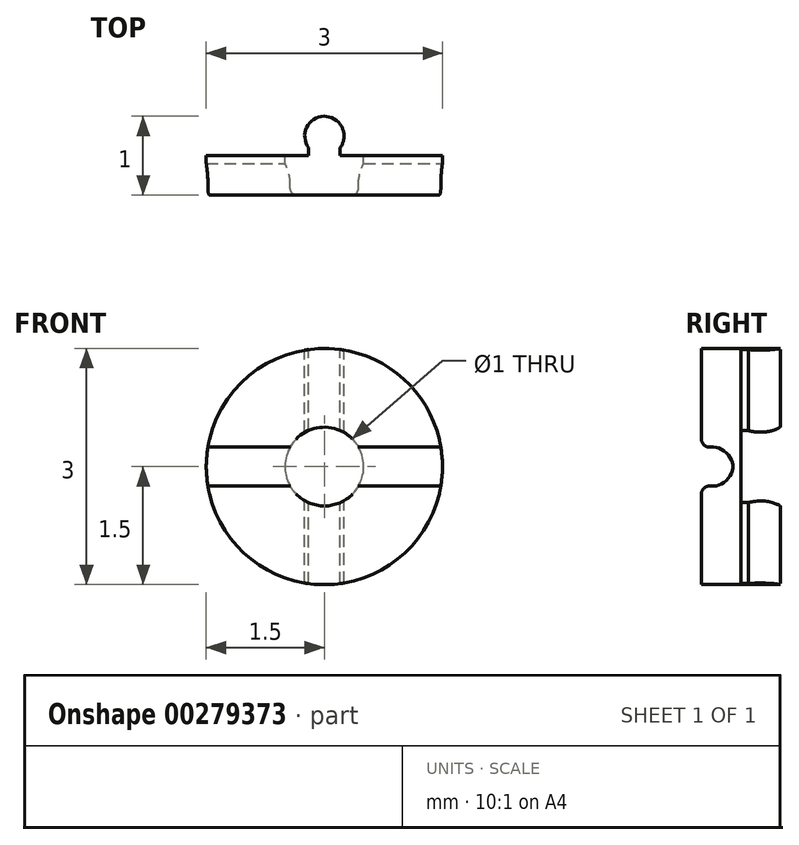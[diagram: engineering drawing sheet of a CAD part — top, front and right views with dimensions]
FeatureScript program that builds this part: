
annotation { "Feature Type Name" : "Feature", "Feature Type Description" : "" }
export const myFeature = defineFeature(function(context is Context, id is Id, definition is map)
    precondition{}
    {
        {
            var Q0;
            Q0=qCreatedBy(makeId("Front.planeOp"),FACE);
            var sketch = newSketch(context, id + "F0", { "sketchPlane" : qUnion([Q0])});
            skCircle(sketch, "E0", {"center": v(0, 0) * mm, "radius": 1.5 * mm});
            skSolve(sketch);
        }
        {
            var Q0;
            Q0 = qSketchRegion(id + "F0", true);
            extrude(context, id + "F1", {"entities" : qUnion([Q0]), "depth" : 1 * mm});
        }
        {
            var Q0;
            Q0=qCreatedBy(makeId("Top.planeOp"),FACE);
            var sketch = newSketch(context, id + "F2", { "sketchPlane" : qUnion([Q0])});
            skArc(sketch, "E1", {"start": v(0.2, -0.4) * mm, "mid": v(0, 0) * mm, "end": v(-0.2, -0.4) * mm});
            skLineSegment(sketch, "E2", {"start": v(0.2, -0.4) * mm, "end": v(1.99, -0.4) * mm});
            skLineSegment(sketch, "E3", {"start": v(1.99, -0.4) * mm, "end": v(1.99, 1) * mm});
            skLineSegment(sketch, "E4", {"start": v(1.99, 1) * mm, "end": v(-1.99, 0.99) * mm});
            skLineSegment(sketch, "E5", {"start": v(-1.99, 0.99) * mm, "end": v(-1.99, -0.4) * mm});
            skLineSegment(sketch, "E6", {"start": v(-1.99, -0.4) * mm, "end": v(-0.2, -0.4) * mm});
            skSolve(sketch);
        }
        {
            var Q0;
            Q0 = qSketchRegion(id + "F2", true);
            extrude(context, id + "F3", {"entities" : qUnion([Q0]), "operationType" : NewBodyOperationType.REMOVE, "endBound" : BoundingType.THROUGH_ALL, "oppositeDirection" : true, "depth" : 25 * mm, "hasSecondDirection" : true, "secondDirectionOppositeDirection" : false, "secondDirectionDepth" : 25 * mm});
        }
        {
            var Q0;
            Q0=qCreatedBy(makeId("Right.planeOp"),FACE);
            var sketch = newSketch(context, id + "F4", { "sketchPlane" : qUnion([Q0])});
            skCircle(sketch, "E7", {"center": v(-0.85, 0) * mm, "radius": 0.25 * mm});
            skSolve(sketch);
        }
        {
            var Q0;
            Q0=makeQuery(id+"F4.imprint","IMPRINT",FACE,{"disambiguationData":[TD([[makeQuery(id+"F4.imprint","IMPRINT",EDGE,{"derivedFrom":sQuery(id+"F4.wireOp",EDGE,"E7")}),1.0]])]});
            extrude(context, id + "F5", {"entities" : qUnion([Q0]), "operationType" : NewBodyOperationType.REMOVE, "endBound" : BoundingType.THROUGH_ALL, "oppositeDirection" : true, "depth" : 25 * mm, "hasSecondDirection" : true, "secondDirectionOppositeDirection" : false, "secondDirectionDepth" : 25 * mm});
        }
        {
            var Q0;
            Q0=makeQuery(id+"F5.boolean.opBoolean","INTERSECT",EDGE,{"disambiguationData":[OD(1.0)],"derivedFrom":[makeQuery(id+"F1.opExtrude","CAP_FACE",FACE,{"disambiguationData":[OSD([sQuery(id+"F0.wireOp",EDGE,"E0")])],"isStart":false}),makeQuery(id+"F5.opExtrude","SWEPT_FACE",FACE,{"disambiguationData":[OSD([sQuery(id+"F4.wireOp",EDGE,"E7")])]})]});
            var Q1;
            Q1=makeQuery(id+"F5.boolean.opBoolean","INTERSECT",EDGE,{"disambiguationData":[OD(0.0)],"derivedFrom":[makeQuery(id+"F1.opExtrude","CAP_FACE",FACE,{"disambiguationData":[OSD([sQuery(id+"F0.wireOp",EDGE,"E0")])],"isStart":false}),makeQuery(id+"F5.opExtrude","SWEPT_FACE",FACE,{"disambiguationData":[OSD([sQuery(id+"F4.wireOp",EDGE,"E7")])]})]});
            fillet(context, id + "F6", {"entities" : qUnion([Q0, Q1]), "radius" : 0.1 * mm, "tangentPropagation" : true, "allowEdgeOverflow" : false});
        }
        {
            var Q0;
            Q0=qCreatedBy(makeId("Front.planeOp"),FACE);
            var sketch = newSketch(context, id + "F7", { "sketchPlane" : qUnion([Q0])});
            skCircle(sketch, "E8", {"center": v(0, 0) * mm, "radius": 0.5 * mm});
            skSolve(sketch);
        }
        {
            var Q0;
            Q0 = qSketchRegion(id + "F7", true);
            extrude(context, id + "F8", {"entities" : qUnion([Q0]), "operationType" : NewBodyOperationType.REMOVE, "endBound" : BoundingType.THROUGH_ALL, "depth" : 25 * mm});
        }
        {
            var Q0;
            Q0=makeQuery(id+"F3.boolean.opBoolean","COPY",FACE,{"derivedFrom":makeQuery(id+"F3.opExtrude","SWEPT_FACE",FACE,{"disambiguationData":[OSD([sQuery(id+"F2.wireOp",EDGE,"E6")])]})});
            var sketch = newSketch(context, id + "F9", { "sketchPlane" : qUnion([Q0])});
            skArc(sketch, "E9.0.0", {"start": v(0.2, -0.46) * mm, "mid": v(0.5, 0) * mm, "end": v(0.2, 0.46) * mm});
            skLineSegment(sketch, "E9.0.1", {"start": v(0.2, -0.46) * mm, "end": v(0.2, -1.49) * mm});
            skArc(sketch, "E9.0.2", {"start": v(0.2, -1.49) * mm, "mid": v(1.5, 0) * mm, "end": v(0.2, 1.49) * mm});
            skLineSegment(sketch, "E9.0.3", {"start": v(0.2, 1.49) * mm, "end": v(0.2, 0.46) * mm});
            skPoint(sketch, "E10.0", {"position": v(1.48, -0.25) * mm});
            skArc(sketch, "E11.0.0", {"start": v(-0.2, 0.46) * mm, "mid": v(-0.5, 0) * mm, "end": v(-0.2, -0.46) * mm});
            skLineSegment(sketch, "E11.0.1", {"start": v(-0.2, 0.46) * mm, "end": v(-0.2, 1.49) * mm});
            skArc(sketch, "E11.0.2", {"start": v(-0.2, 1.49) * mm, "mid": v(-1.5, 0) * mm, "end": v(-0.2, -1.49) * mm});
            skLineSegment(sketch, "E11.0.3", {"start": v(-0.2, -1.49) * mm, "end": v(-0.2, -0.46) * mm});
            skSolve(sketch);
        }
        {
            var Q0;
            Q0 = qSketchRegion(id + "F9", true);
            extrude(context, id + "F10", {"entities" : qUnion([Q0]), "operationType" : NewBodyOperationType.REMOVE, "oppositeDirection" : true, "depth" : 0.1 * mm});
        }
    });
